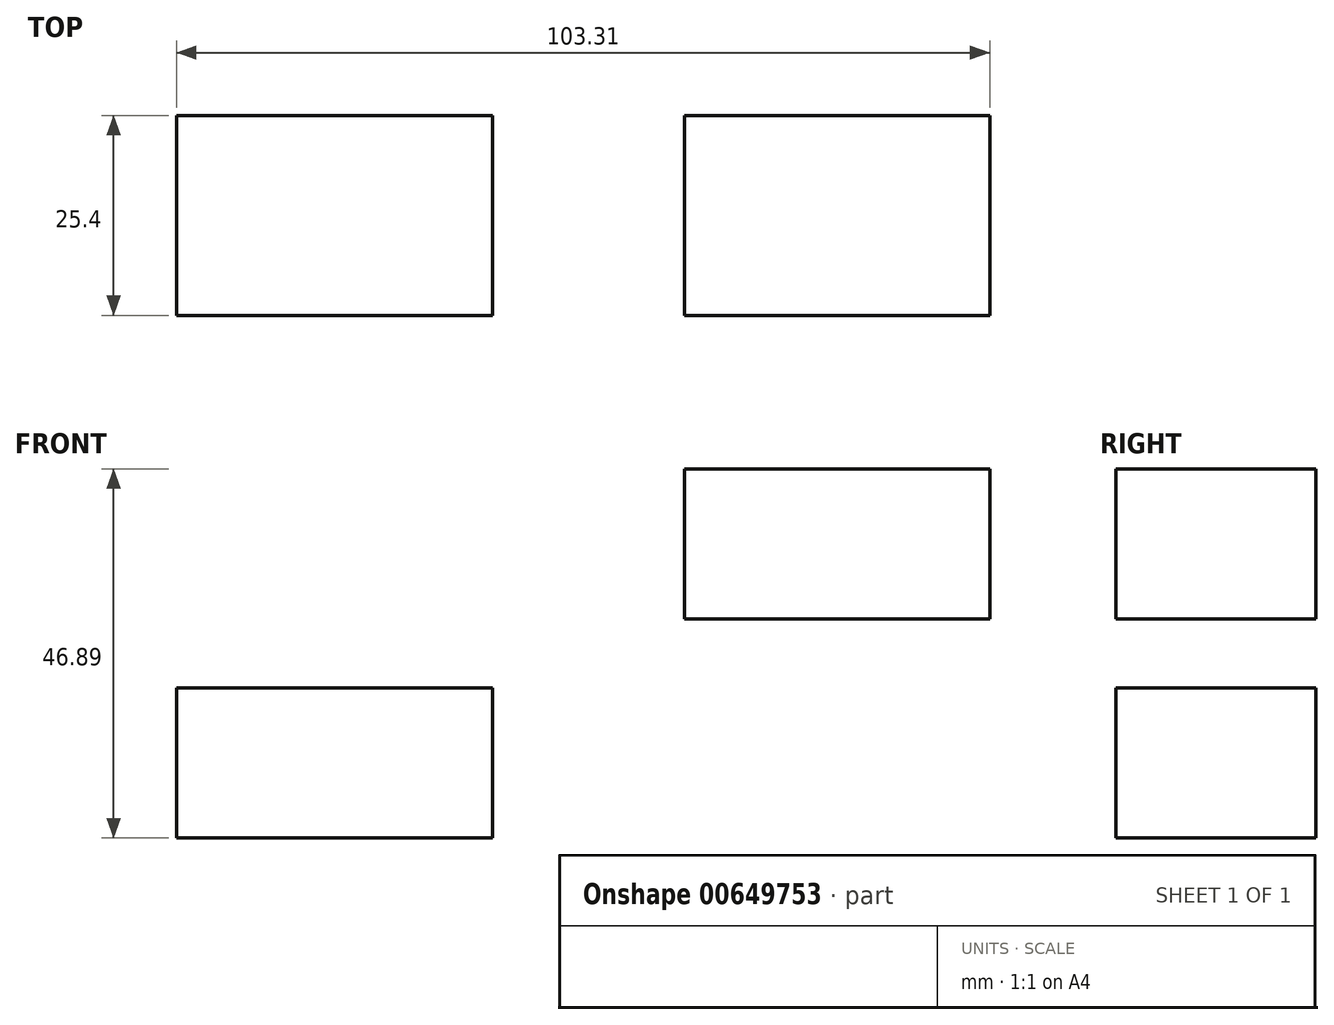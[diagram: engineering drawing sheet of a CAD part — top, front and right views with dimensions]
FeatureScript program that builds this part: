
annotation { "Feature Type Name" : "Feature", "Feature Type Description" : "" }
export const myFeature = defineFeature(function(context is Context, id is Id, definition is map)
    precondition{}
    {
        {
            var Q0;
            Q0=qCreatedBy(makeId("Front.planeOp"),FACE);
            var sketch = newSketch(context, id + "F0", { "sketchPlane" : qUnion([Q0])});
            skLineSegment(sketch, "E0.bottom", {"start": v(0, 0) * mm, "end": v(40.17, 0) * mm});
            skLineSegment(sketch, "E0.top", {"start": v(0, 19.07) * mm, "end": v(40.17, 19.07) * mm});
            skLineSegment(sketch, "E0.left", {"start": v(0, 0) * mm, "end": v(0, 19.07) * mm});
            skLineSegment(sketch, "E0.right", {"start": v(40.17, 0) * mm, "end": v(40.17, 19.07) * mm});
            skLineSegment(sketch, "E1.bottom", {"start": v(64.55, 46.89) * mm, "end": v(103.3, 46.89) * mm});
            skLineSegment(sketch, "E1.top", {"start": v(64.55, 27.82) * mm, "end": v(103.3, 27.82) * mm});
            skLineSegment(sketch, "E1.left", {"start": v(64.55, 46.89) * mm, "end": v(64.55, 27.82) * mm});
            skLineSegment(sketch, "E1.right", {"start": v(103.3, 46.89) * mm, "end": v(103.3, 27.82) * mm});
            skSolve(sketch);
        }
        {
            var Q0;
            Q0 = qSketchRegion(id + "F0", true);
            extrude(context, id + "F1", {"entities" : qUnion([Q0]), "depth" : 25.4 * mm, "offsetDistance" : 25.4 * mm});
        }
    });
